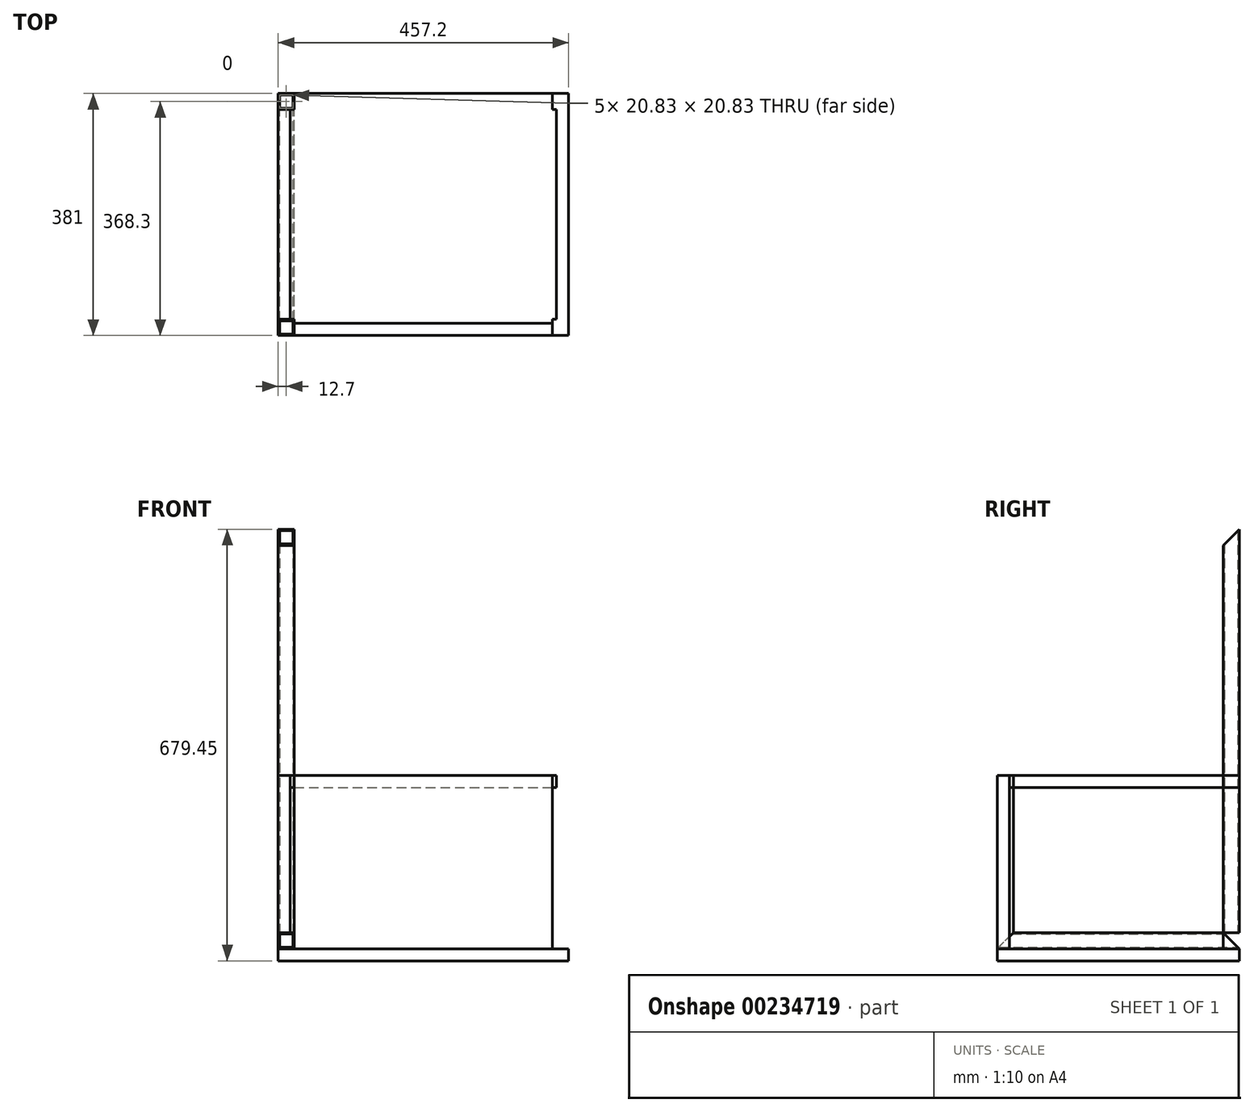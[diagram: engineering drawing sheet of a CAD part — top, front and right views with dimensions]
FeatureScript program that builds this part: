
annotation { "Feature Type Name" : "Feature", "Feature Type Description" : "" }
export const myFeature = defineFeature(function(context is Context, id is Id, definition is map)
    precondition{}
    {
        {
            var Q0;
            Q0=qCreatedBy(makeId("Top.planeOp"),FACE);
            var sketch = newSketch(context, id + "F0", { "sketchPlane" : qUnion([Q0])});
            skLineSegment(sketch, "E0.bottom", {"start": v(25.4, 0) * mm, "end": v(0, 0) * mm});
            skLineSegment(sketch, "E0.top", {"start": v(25.4, -25.4) * mm, "end": v(0, -25.4) * mm});
            skLineSegment(sketch, "E0.left", {"start": v(25.4, 0) * mm, "end": v(25.4, -25.4) * mm});
            skLineSegment(sketch, "E0.right", {"start": v(0, 0) * mm, "end": v(0, -25.4) * mm});
            skLineSegment(sketch, "E1.bottom", {"start": v(2.29, -23.11) * mm, "end": v(23.11, -23.11) * mm});
            skLineSegment(sketch, "E1.top", {"start": v(2.29, -2.29) * mm, "end": v(23.11, -2.29) * mm});
            skLineSegment(sketch, "E1.left", {"start": v(2.29, -23.11) * mm, "end": v(2.29, -2.29) * mm});
            skLineSegment(sketch, "E1.right", {"start": v(23.11, -23.11) * mm, "end": v(23.11, -2.29) * mm});
            skSolve(sketch);
        }
        {
            var Q0;
            Q0=makeQuery(id+"F0.imprint","IMPRINT",FACE,{"disambiguationData":[TD([[makeQuery(id+"F0.imprint","IMPRINT",EDGE,{"derivedFrom":sQuery(id+"F0.wireOp",EDGE,"E0.bottom")}),1.0]])]});
            extrude(context, id + "F1", {"entities" : qUnion([Q0]), "depth" : 660.4 * mm});
        }
        {
            var Q0;
            Q0=qCreatedBy(makeId("Right.planeOp"),FACE);
            var sketch = newSketch(context, id + "F2", { "sketchPlane" : qUnion([Q0])});
            skLineSegment(sketch, "E2", {"start": v(0, 0) * mm, "end": v(-25.4, 0) * mm});
            skLineSegment(sketch, "E3", {"start": v(-25.4, 25.4) * mm, "end": v(0, 0) * mm});
            skLineSegment(sketch, "E4", {"start": v(-25.4, 0) * mm, "end": v(-25.4, 25.4) * mm});
            skSolve(sketch);
        }
        {
            var Q0;
            Q0=makeQuery(id+"F2.imprint","IMPRINT",FACE,{"disambiguationData":[TD([[makeQuery(id+"F2.imprint","IMPRINT",EDGE,{"derivedFrom":sQuery(id+"F2.wireOp",EDGE,"E2")}),-1.0]])]});
            extrude(context, id + "F3", {"entities" : qUnion([Q0]), "operationType" : NewBodyOperationType.REMOVE, "depth" : 25.4 * mm});
        }
        {
            var Q0;
            Q0=makeQuery(id+"F1.opExtrude","SWEPT_FACE",FACE,{"disambiguationData":[OSD([sQuery(id+"F0.wireOp",EDGE,"E0.right")])]});
            var sketch = newSketch(context, id + "F4", { "sketchPlane" : qUnion([Q0])});
            skLineSegment(sketch, "E5", {"start": v(0, 660.4) * mm, "end": v(25.4, 635) * mm});
            skLineSegment(sketch, "E6", {"start": v(25.4, 635) * mm, "end": v(25.4, 660.4) * mm});
            skLineSegment(sketch, "E7", {"start": v(25.4, 660.4) * mm, "end": v(0, 660.4) * mm});
            skSolve(sketch);
        }
        {
            var Q0;
            Q0=makeQuery(id+"F4.imprint","IMPRINT",FACE,{"disambiguationData":[TD([[makeQuery(id+"F4.imprint","IMPRINT",EDGE,{"derivedFrom":sQuery(id+"F4.wireOp",EDGE,"E5")}),1.0]])]});
            var Q1;
            Q1=makeQuery(id+"F1.opExtrude","SWEPT_FACE",FACE,{"disambiguationData":[OSD([sQuery(id+"F0.wireOp",EDGE,"E0.left")])]});
            extrude(context, id + "F5", {"entities" : qUnion([Q0]), "operationType" : NewBodyOperationType.REMOVE, "endBound" : BoundingType.UP_TO_SURFACE, "oppositeDirection" : true, "endBoundEntityFace" : qUnion([Q1]), "depth" : 25.4 * mm});
        }
        {
            var Q0;
            Q0=qCreatedBy(makeId("Front.planeOp"),FACE);
            var sketch = newSketch(context, id + "F6", { "sketchPlane" : qUnion([Q0])});
            skLineSegment(sketch, "E8.bottom", {"start": v(0, 0) * mm, "end": v(25.4, 0) * mm});
            skLineSegment(sketch, "E8.top", {"start": v(0, 25.4) * mm, "end": v(25.4, 25.4) * mm});
            skLineSegment(sketch, "E8.left", {"start": v(0, 0) * mm, "end": v(0, 25.4) * mm});
            skLineSegment(sketch, "E8.right", {"start": v(25.4, 0) * mm, "end": v(25.4, 25.4) * mm});
            skLineSegment(sketch, "E9.0", {"start": v(23.11, 2.29) * mm, "end": v(23.11, 23.11) * mm});
            skLineSegment(sketch, "E9.1", {"start": v(2.29, 2.29) * mm, "end": v(23.11, 2.29) * mm});
            skLineSegment(sketch, "E9.2", {"start": v(2.29, 2.29) * mm, "end": v(2.29, 23.11) * mm});
            skLineSegment(sketch, "E9.3", {"start": v(2.29, 23.11) * mm, "end": v(23.11, 23.11) * mm});
            skSolve(sketch);
        }
        {
            var Q0;
            Q0 = qSketchRegion(id + "F6", true);
            extrude(context, id + "F7", {"entities" : qUnion([Q0]), "depth" : 381 * mm});
        }
        {
            var Q0;
            Q0=makeQuery(id+"F7.opExtrude","SWEPT_FACE",FACE,{"disambiguationData":[OSD([sQuery(id+"F6.wireOp",EDGE,"E8.left")])]});
            var sketch = newSketch(context, id + "F8", { "sketchPlane" : qUnion([Q0])});
            skLineSegment(sketch, "E10", {"start": v(0, 0) * mm, "end": v(0, 25.4) * mm});
            skLineSegment(sketch, "E11", {"start": v(0, 25.4) * mm, "end": v(25.4, 25.4) * mm});
            skLineSegment(sketch, "E12", {"start": v(25.4, 25.4) * mm, "end": v(0, 0) * mm});
            skLineSegment(sketch, "E13", {"start": v(381, 0) * mm, "end": v(381, 25.4) * mm});
            skLineSegment(sketch, "E14", {"start": v(381, 25.4) * mm, "end": v(355.6, 25.4) * mm});
            skLineSegment(sketch, "E15", {"start": v(355.6, 25.4) * mm, "end": v(381, 0) * mm});
            skSolve(sketch);
        }
        {
            var Q0;
            Q0=makeQuery(id+"F8.imprint","IMPRINT",FACE,{"disambiguationData":[TD([[makeQuery(id+"F8.imprint","IMPRINT",EDGE,{"derivedFrom":sQuery(id+"F8.wireOp",EDGE,"E13")}),1.0]])]});
            var Q1;
            Q1=makeQuery(id+"F8.imprint","IMPRINT",FACE,{"disambiguationData":[TD([[makeQuery(id+"F8.imprint","IMPRINT",EDGE,{"derivedFrom":sQuery(id+"F8.wireOp",EDGE,"E10")}),-1.0]])]});
            var Q2;
            Q2=makeQuery(id+"F7.opExtrude","SWEPT_FACE",FACE,{"disambiguationData":[OSD([sQuery(id+"F6.wireOp",EDGE,"E8.right")])]});
            extrude(context, id + "F9", {"entities" : qUnion([Q0, Q1]), "operationType" : NewBodyOperationType.REMOVE, "endBound" : BoundingType.UP_TO_SURFACE, "oppositeDirection" : true, "endBoundEntityFace" : qUnion([Q2]), "depth" : 25.4 * mm});
        }
        {
            var Q0;
            Q0=qCreatedBy(makeId("Top.planeOp"),FACE);
            var sketch = newSketch(context, id + "F10", { "sketchPlane" : qUnion([Q0])});
            skLineSegment(sketch, "E16.bottom", {"start": v(0, 0) * mm, "end": v(457.2, 0) * mm});
            skLineSegment(sketch, "E16.top", {"start": v(0, -381) * mm, "end": v(457.2, -381) * mm});
            skLineSegment(sketch, "E16.left", {"start": v(0, 0) * mm, "end": v(0, -381) * mm});
            skLineSegment(sketch, "E16.right", {"start": v(457.2, 0) * mm, "end": v(457.2, -381) * mm});
            skSolve(sketch);
        }
        {
            var Q0;
            Q0=makeQuery(id+"F10.imprint","IMPRINT",FACE,{"disambiguationData":[TD([[makeQuery(id+"F10.imprint","IMPRINT",EDGE,{"derivedFrom":sQuery(id+"F10.wireOp",EDGE,"E16.bottom")}),-1.0]])]});
            extrude(context, id + "F11", {"entities" : qUnion([Q0]), "oppositeDirection" : true, "depth" : 19.05 * mm});
        }
        {
            var Q0;
            Q0=qCreatedBy(makeId("Top.planeOp"),FACE);
            cPlane(context, id + "F12", {"entities" : qUnion([Q0]), "cplaneType" : CPlaneType.OFFSET, "offset" : 254 * mm, "width" : 152.4 * mm, "height" : 152.4 * mm});
        }
        {
            var Q0;
            Q0=qCreatedBy(id+"F12.planeOp",FACE);
            var sketch = newSketch(context, id + "F13", { "sketchPlane" : qUnion([Q0])});
            skLineSegment(sketch, "E17.0", {"start": v(25.4, 0) * mm, "end": v(25.4, -25.4) * mm});
            skLineSegment(sketch, "E18.0.1", {"start": v(25.4, -25.4) * mm, "end": v(19.05, -25.4) * mm});
            skLineSegment(sketch, "E18.0.3", {"start": v(19.05, -25.4) * mm, "end": v(25.4, -25.4) * mm});
            skLineSegment(sketch, "E19.0", {"start": v(25.4, 0) * mm, "end": v(431.8, 0) * mm});
            skLineSegment(sketch, "E20.0", {"start": v(25.4, -355.6) * mm, "end": v(19.05, -355.6) * mm});
            skLineSegment(sketch, "E21.0", {"start": v(25.4, -361.95) * mm, "end": v(25.4, -355.6) * mm});
            skPoint(sketch, "E22.orphan", {"position": v(0, -381) * mm});
            skLineSegment(sketch, "E23.top", {"start": v(438.15, -355.6) * mm, "end": v(431.8, -355.6) * mm});
            skLineSegment(sketch, "E23.right", {"start": v(431.8, -361.95) * mm, "end": v(431.8, -355.6) * mm});
            skPoint(sketch, "E23.bottom.start.orphan", {"position": v(457.2, -381) * mm});
            skLineSegment(sketch, "E24.top", {"start": v(438.15, -25.4) * mm, "end": v(431.8, -25.4) * mm});
            skLineSegment(sketch, "E24.right", {"start": v(431.8, 0) * mm, "end": v(431.8, -25.4) * mm});
            skPoint(sketch, "E24.bottom.start.orphan", {"position": v(457.2, 0) * mm});
            skPoint(sketch, "E25.orphan", {"position": v(0, 0) * mm});
            skLineSegment(sketch, "E26.0", {"start": v(25.4, -361.95) * mm, "end": v(431.8, -361.95) * mm});
            skPoint(sketch, "E27.orphan", {"position": v(25.4, -381) * mm});
            skLineSegment(sketch, "E28.0", {"start": v(19.05, -355.6) * mm, "end": v(19.05, -25.4) * mm});
            skPoint(sketch, "E29.0.end.orphan", {"position": v(0, -25.4) * mm});
            skPoint(sketch, "E29.0.start.orphan", {"position": v(0, -355.6) * mm});
            skLineSegment(sketch, "E30.0", {"start": v(438.15, -25.4) * mm, "end": v(438.15, -355.6) * mm});
            skSolve(sketch);
        }
        {
            var Q0;
            {var subQ0=sQuery(id+"F13.wireOp",EDGE,"E17.0");Q0=makeQuery(id+"F13.imprint","IMPRINT",FACE,{"disambiguationData":[TD([[makeQuery(id+"F13.imprint","IMPRINT",EDGE,{"derivedFrom":subQ0}),1.0]])]});}
            extrude(context, id + "F14", {"entities" : qUnion([Q0]), "depth" : 19.05 * mm});
        }
        {
            var Q0;
            Q0=qCreatedBy(makeId("Right.planeOp"),FACE);
            var sketch = newSketch(context, id + "F15", { "sketchPlane" : qUnion([Q0])});
            skLineSegment(sketch, "E31.bottom", {"start": v(-25.4, 25.4) * mm, "end": v(-355.6, 25.4) * mm});
            skLineSegment(sketch, "E31.top", {"start": v(-25.4, 273.05) * mm, "end": v(-355.6, 273.05) * mm});
            skLineSegment(sketch, "E31.left", {"start": v(-25.4, 25.4) * mm, "end": v(-25.4, 273.05) * mm});
            skLineSegment(sketch, "E31.right", {"start": v(-355.6, 25.4) * mm, "end": v(-355.6, 273.05) * mm});
            skSolve(sketch);
        }
        {
            var Q0;
            Q0=makeQuery(id+"F15.imprint","IMPRINT",FACE,{"disambiguationData":[TD([[makeQuery(id+"F15.imprint","IMPRINT",EDGE,{"derivedFrom":sQuery(id+"F15.wireOp",EDGE,"E31.bottom")}),-1.0]])]});
            extrude(context, id + "F16", {"entities" : qUnion([Q0]), "depth" : 19.05 * mm});
        }
        {
            var Q0;
            Q0=makeQuery(id+"F11.opExtrude","SWEPT_FACE",FACE,{"disambiguationData":[OSD([sQuery(id+"F10.wireOp",EDGE,"E16.top")])]});
            var sketch = newSketch(context, id + "F17", { "sketchPlane" : qUnion([Q0])});
            skLineSegment(sketch, "E32.bottom", {"start": v(25.4, 0) * mm, "end": v(431.8, 0) * mm});
            skLineSegment(sketch, "E32.top", {"start": v(25.4, 273.05) * mm, "end": v(431.8, 273.05) * mm});
            skLineSegment(sketch, "E32.left", {"start": v(25.4, 0) * mm, "end": v(25.4, 273.05) * mm});
            skLineSegment(sketch, "E32.right", {"start": v(431.8, 0) * mm, "end": v(431.8, 273.05) * mm});
            skSolve(sketch);
        }
        {
            var Q0;
            Q0=makeQuery(id+"F17.imprint","IMPRINT",FACE,{"disambiguationData":[TD([[makeQuery(id+"F17.imprint","IMPRINT",EDGE,{"derivedFrom":sQuery(id+"F17.wireOp",EDGE,"E32.bottom")}),1.0]])]});
            extrude(context, id + "F18", {"entities" : qUnion([Q0]), "oppositeDirection" : true, "depth" : 19.05 * mm});
        }
    });
